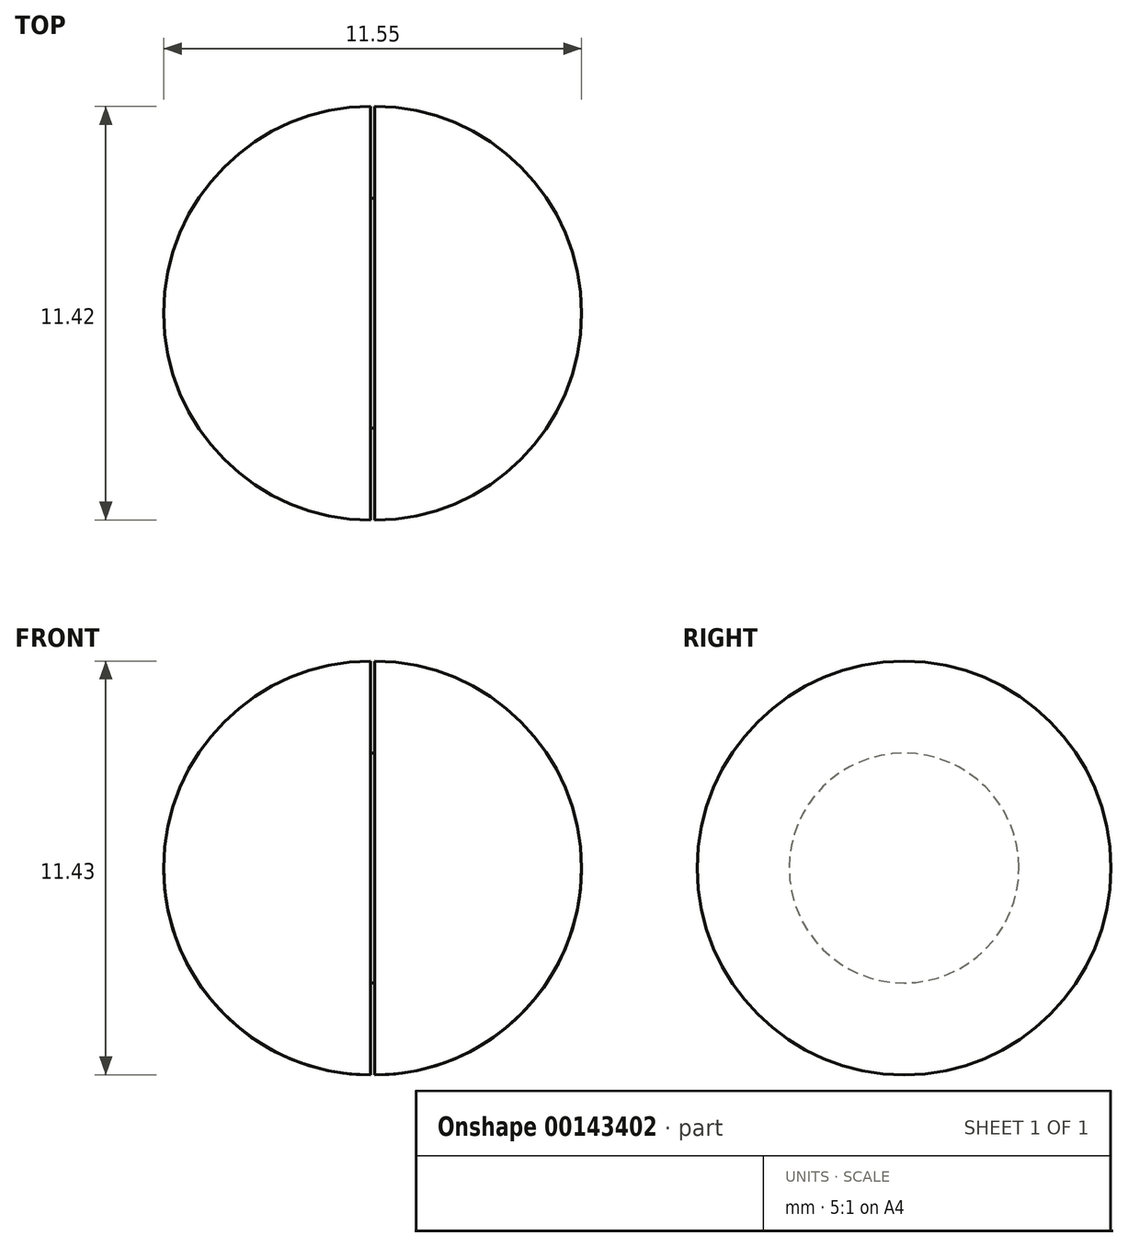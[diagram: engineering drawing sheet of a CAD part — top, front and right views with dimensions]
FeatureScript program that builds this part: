
annotation { "Feature Type Name" : "Feature", "Feature Type Description" : "" }
export const myFeature = defineFeature(function(context is Context, id is Id, definition is map)
    precondition{}
    {
        {
            var Q0;
            Q0=qCreatedBy(makeId("Right.planeOp"),FACE);
            var sketch = newSketch(context, id + "F0", { "sketchPlane" : qUnion([Q0])});
            skCircle(sketch, "E0", {"center": v(0, 0) * mm, "radius": 3.18 * mm});
            skSolve(sketch);
        }
        {
            var Q0;
            Q0=makeQuery(id+"F0.imprint","IMPRINT",FACE,{"disambiguationData":[TD([[makeQuery(id+"F0.imprint","IMPRINT",EDGE,{"derivedFrom":sQuery(id+"F0.wireOp",EDGE,"E0")}),1.0]])]});
            var Q1;
            Q1 = qSketchRegion(id + "F2", true);
            extrude(context, id + "F1", {"entities" : qUnion([Q0, Q1]), "oppositeDirection" : true, "depth" : 2.9 / 50.8 * mm});
        }
        {
            var Q0;
            Q0=qCreatedBy(makeId("Front.planeOp"),FACE);
            var sketch = newSketch(context, id + "F2", { "sketchPlane" : qUnion([Q0])});
            skLineSegment(sketch, "E1", {"start": v(0, -3.18) * mm, "end": v(-73.66, -3.18) * mm});
            skLineSegment(sketch, "E2", {"start": v(-73.66, 3.18) * mm, "end": v(0, 3.18) * mm});
            skLineSegment(sketch, "E3", {"start": v(0, 0) * mm, "end": v(0, 5.72) * mm});
            skArc(sketch, "E4", {"start": v(5.72, 0) * mm, "mid": v(4.04, 4.04) * mm, "end": v(0, 5.72) * mm});
            skLineSegment(sketch, "E5", {"start": v(5.72, 0) * mm, "end": v(0, 0) * mm});
            skSolve(sketch);
        }
        {
            var Q0;
            {var subQ3=sQuery(id+"F2.wireOp",EDGE,"E4");Q0=makeQuery(id+"F2.imprint","IMPRINT",FACE,{"disambiguationData":[TD([[makeQuery(id+"F2.imprint","IMPRINT",EDGE,{"derivedFrom":subQ3}),1.0]])]});}
            var Q1;
            Q1=makeQuery(id+"F1.opExtrude","SWEPT_FACE",FACE,{"disambiguationData":[OSD([sQuery(id+"F0.wireOp",EDGE,"E0")])]});
            revolve(context, id + "F3", {"operationType" : NewBodyOperationType.ADD, "entities" : qUnion([Q0]), "axis" : qUnion([Q1]), "revolveType" : RevolveType.FULL});
        }
        {
            var Q0;
            Q0=makeQuery(id+"F1.opExtrude","SWEPT_BODY",BODY,{"disambiguationData":[OSD([sQuery(id+"F0.wireOp",EDGE,"E0")])]});
            var Q1;
            Q1=makeQuery(id+"F1.opExtrude","CAP_FACE",FACE,{"disambiguationData":[OSD([sQuery(id+"F0.wireOp",EDGE,"E0")])],"isStart":false});
            mirror(context, id + "F4", {"operationType" : NewBodyOperationType.ADD, "entities" : qUnion([Q0]), "mirrorPlane" : qUnion([Q1])});
        }
    });
